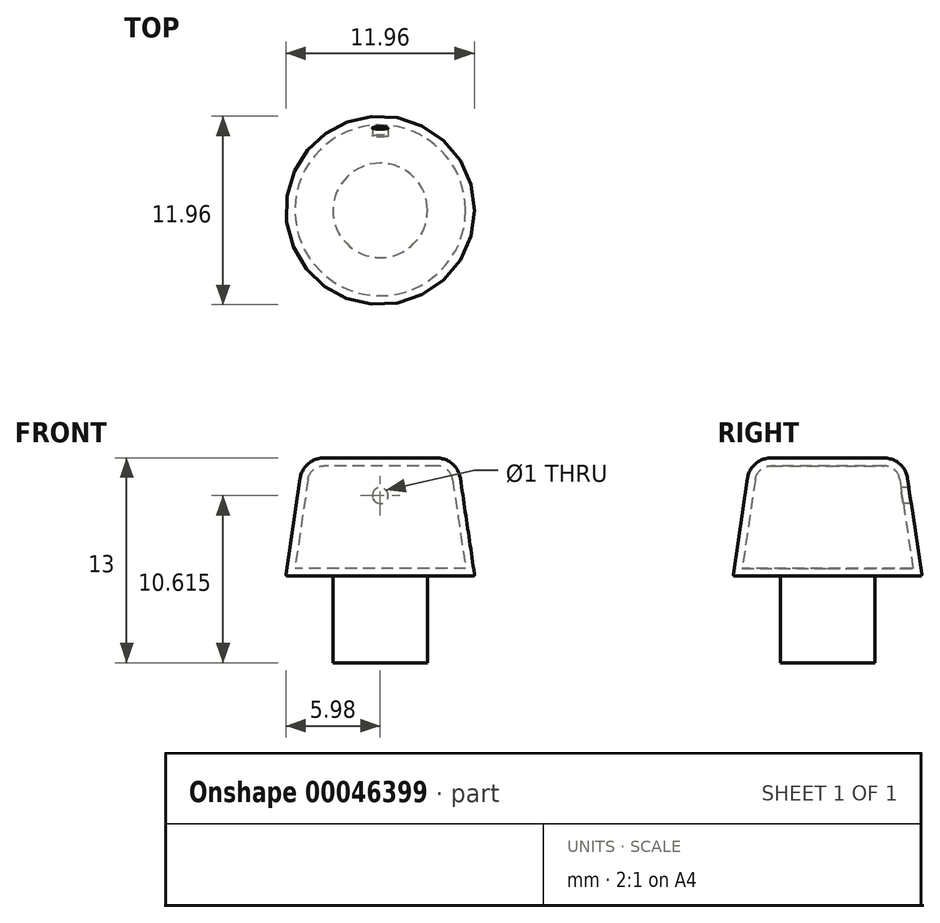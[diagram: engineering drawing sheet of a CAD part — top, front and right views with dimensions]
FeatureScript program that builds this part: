
annotation { "Feature Type Name" : "Feature", "Feature Type Description" : "" }
export const myFeature = defineFeature(function(context is Context, id is Id, definition is map)
    precondition{}
    {
        {
            var Q0;
            Q0=qCreatedBy(makeId("Front.planeOp"),FACE);
            var sketch = newSketch(context, id + "F0", { "sketchPlane" : qUnion([Q0])});
            skLineSegment(sketch, "E0", {"start": v(0, 0) * mm, "end": v(5.42, 0) * mm});
            skLineSegment(sketch, "E1", {"start": v(5.42, 0) * mm, "end": v(4.59, 5.65) * mm});
            skLineSegment(sketch, "E2", {"start": v(3.6, 6.5) * mm, "end": v(0, 6.5) * mm});
            skPoint(sketch, "E3.visualSharp", {"position": v(4.46, 6.5) * mm});
            skArc(sketch, "E3.filletArc", {"start": v(4.59, 5.65) * mm, "mid": v(4.25, 6.26) * mm, "end": v(3.6, 6.5) * mm});
            skPoint(sketch, "E4.visualSharp", {"position": v(5.42, 0) * mm});
            skLineSegment(sketch, "E5", {"start": v(0, 6.5) * mm, "end": v(0, 0) * mm, "construction": true});
            skLineSegment(sketch, "E6.0", {"start": v(3.6, 7) * mm, "end": v(0, 7) * mm});
            skArc(sketch, "E6.1", {"start": v(5.08, 5.72) * mm, "mid": v(4.58, 6.64) * mm, "end": v(3.6, 7) * mm});
            skLineSegment(sketch, "E6.2", {"start": v(5.98, -0.39) * mm, "end": v(5.08, 5.72) * mm});
            skLineSegment(sketch, "E6.3", {"start": v(0, -0.5) * mm, "end": v(3, -0.5) * mm, "construction": true});
            skLineSegment(sketch, "E7", {"start": v(0, -0.5) * mm, "end": v(0, 0) * mm});
            skLineSegment(sketch, "E8", {"start": v(0, 6.5) * mm, "end": v(0, 7) * mm});
            skLineSegment(sketch, "E9.bottom", {"start": v(0, -6) * mm, "end": v(3, -6) * mm});
            skLineSegment(sketch, "E9.left", {"start": v(0, -6) * mm, "end": v(0, -0.5) * mm});
            skLineSegment(sketch, "E9.right", {"start": v(3, -6) * mm, "end": v(3, -0.5) * mm});
            skLineSegment(sketch, "E10", {"start": v(3, -0.5) * mm, "end": v(5.88, -0.5) * mm});
            skPoint(sketch, "E11.visualSharp", {"position": v(6, -0.5) * mm});
            skArc(sketch, "E11.filletArc", {"start": v(5.88, -0.5) * mm, "mid": v(5.96, -0.47) * mm, "end": v(5.98, -0.39) * mm});
            skSolve(sketch);
        }
        {
            var Q0;
            Q0=makeQuery(id+"F0.imprint","IMPRINT",FACE,{"disambiguationData":[TD([[makeQuery(id+"F0.imprint","IMPRINT",EDGE,{"derivedFrom":sQuery(id+"F0.wireOp",EDGE,"E0")}),-1.0]])]});
            var Q1;
            Q1=sQuery(id+"F0.wireOp",EDGE,"E5");
            revolve(context, id + "F1", {"entities" : qUnion([Q0]), "axis" : qUnion([Q1]), "revolveType" : RevolveType.FULL});
        }
        {
            var Q0;
            Q0=qCreatedBy(makeId("Front.planeOp"),FACE);
            var sketch = newSketch(context, id + "F2", { "sketchPlane" : qUnion([Q0])});
            skCircle(sketch, "E12", {"center": v(0, 4.61) * mm, "radius": 0.5 * mm});
            skSolve(sketch);
        }
        {
            var Q0;
            Q0=makeQuery(id+"F2.imprint","IMPRINT",FACE,{"disambiguationData":[TD([[makeQuery(id+"F2.imprint","IMPRINT",EDGE,{"derivedFrom":sQuery(id+"F2.wireOp",EDGE,"E12")}),1.0]])]});
            extrude(context, id + "F3", {"entities" : qUnion([Q0]), "operationType" : NewBodyOperationType.REMOVE, "oppositeDirection" : true, "depth" : 25 * mm});
        }
    });
